# Revit family: Sanitary_Dispenser_Dandent_MGH100_Cup-Dispenser
name_source: partatom
category: Furniture
revit_build: Autodesk Revit 2017 (Build: 20190508_0315(x64)
units: mm (PartAtom-declared; Revit-internal decimal feet)

## family parameters
Always vertical = Yes
Cut with Voids When Loaded = No
OmniClass Number = 23.40.70.11.14.21
OmniClass Title = Health Care Furniture
Room Calculation Point = No
Shared = No
Work Plane-Based = No

## types (1)
- Cup dispenser - MGH100
    AssetType = Movable
    BIMObjectName = Sanitary_Dispenser_Dandent_MGH100_Cup-Dispenser
    Brand = Dandent
    Category = Cup dispenser
    Color = White
    ConvergoRefNr = 0151-1909-0007-SE
    Cost = 0 $
    DispenserSecondaryMaterial = Plastic, Opaque White
    DurationUnit = Year
    Finish = Front in white or compact laminate wood. Available in beech, birch and oak.
    IfcExportAs = IfcFurnitureType
    IfcExportType = UNDEFINED
    MainColor = White
    Manufacturer = Dandent
    ManufacturerName = Dandent
    ManufacturerURL = https://www.dandent.se
    Material = Plastic, wood
    Model = Cup dispenser - MGH100
    ModelNumber = MGH100
    NBSDescription = Paper roll dispensers
    NBSReference = 45-35-72/342
    Name = Dandent_MGH100_Cup-Dispenser
    NominalDepth = 116 mm  [stored 0.380577 ft]
    NominalHeight = 408 mm
    NominalLength = 110 mm
    Product data url = https://www.bimobject.com
    Shape = Rectangular
    Size = 111x113x400 mm
    URL = https://www.dandent.se
    Uniclass2 = Pr_40_30_76
    Uniclass2015Description = Sanitary accessories
    Uniclass2015Reference = Pr_40_20_76
    Version = 1
    VersionDate = 12/09/2019
    WarrantyDurationUnit = Year

note: [stored X ft] marks values corroborated as IEEE doubles in the binary element streams (Revit-internal decimal feet)

## geometry (parser evidence)
native form markers: Sweep x4
no freeform markers — native parametric forms only
